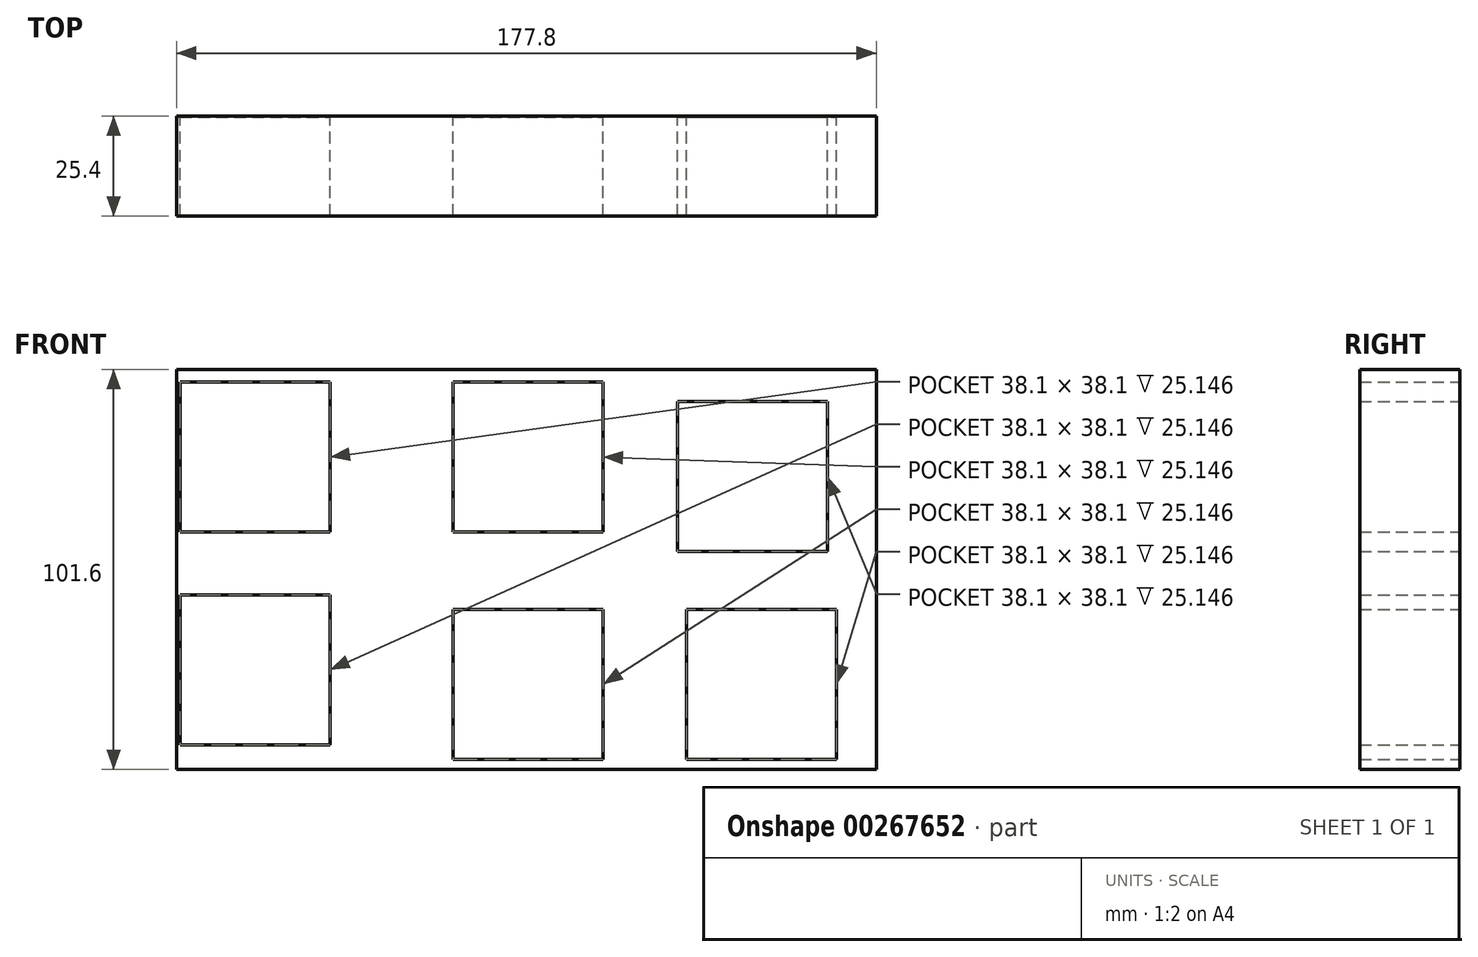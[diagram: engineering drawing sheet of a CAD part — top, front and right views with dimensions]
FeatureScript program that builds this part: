
annotation { "Feature Type Name" : "Feature", "Feature Type Description" : "" }
export const myFeature = defineFeature(function(context is Context, id is Id, definition is map)
    precondition{}
    {
        {
            var Q0;
            Q0=qCreatedBy(makeId("Front.planeOp"),FACE);
            var sketch = newSketch(context, id + "F0", { "sketchPlane" : qUnion([Q0])});
            skLineSegment(sketch, "E0.bottom", {"start": v(-82.35, 60.96) * mm, "end": v(95.45, 60.96) * mm});
            skLineSegment(sketch, "E0.top", {"start": v(-82.35, -40.64) * mm, "end": v(95.45, -40.64) * mm});
            skLineSegment(sketch, "E0.left", {"start": v(-82.35, 60.96) * mm, "end": v(-82.35, -40.64) * mm});
            skLineSegment(sketch, "E0.right", {"start": v(95.45, 60.96) * mm, "end": v(95.45, -40.64) * mm});
            skLineSegment(sketch, "E1.bottom", {"start": v(-81.47, 57.78) * mm, "end": v(-43.37, 57.78) * mm});
            skLineSegment(sketch, "E1.top", {"start": v(-81.47, 19.68) * mm, "end": v(-43.37, 19.68) * mm});
            skLineSegment(sketch, "E1.left", {"start": v(-81.47, 57.78) * mm, "end": v(-81.47, 19.68) * mm});
            skLineSegment(sketch, "E1.right", {"start": v(-43.37, 57.78) * mm, "end": v(-43.37, 19.68) * mm});
            skLineSegment(sketch, "E2.bottom", {"start": v(-81.47, 3.74) * mm, "end": v(-43.37, 3.74) * mm});
            skLineSegment(sketch, "E2.top", {"start": v(-81.47, -34.36) * mm, "end": v(-43.37, -34.36) * mm});
            skLineSegment(sketch, "E2.left", {"start": v(-81.47, 3.74) * mm, "end": v(-81.47, -34.36) * mm});
            skLineSegment(sketch, "E2.right", {"start": v(-43.37, 3.74) * mm, "end": v(-43.37, -34.36) * mm});
            skLineSegment(sketch, "E3.bottom", {"start": v(-12.03, 57.78) * mm, "end": v(26.07, 57.78) * mm});
            skLineSegment(sketch, "E3.top", {"start": v(-12.03, 19.68) * mm, "end": v(26.07, 19.68) * mm});
            skLineSegment(sketch, "E3.left", {"start": v(-12.03, 57.78) * mm, "end": v(-12.03, 19.68) * mm});
            skLineSegment(sketch, "E3.right", {"start": v(26.07, 57.78) * mm, "end": v(26.07, 19.68) * mm});
            skLineSegment(sketch, "E4.bottom", {"start": v(-12.03, 0) * mm, "end": v(26.07, 0) * mm});
            skLineSegment(sketch, "E4.top", {"start": v(-12.03, -38.1) * mm, "end": v(26.07, -38.1) * mm});
            skLineSegment(sketch, "E4.left", {"start": v(-12.03, 0) * mm, "end": v(-12.03, -38.1) * mm});
            skLineSegment(sketch, "E4.right", {"start": v(26.07, 0) * mm, "end": v(26.07, -38.1) * mm});
            skLineSegment(sketch, "E5.bottom", {"start": v(47.18, 0) * mm, "end": v(85.28, 0) * mm});
            skLineSegment(sketch, "E5.top", {"start": v(47.18, -38.1) * mm, "end": v(85.28, -38.1) * mm});
            skLineSegment(sketch, "E5.left", {"start": v(47.18, 0) * mm, "end": v(47.18, -38.1) * mm});
            skLineSegment(sketch, "E5.right", {"start": v(85.28, 0) * mm, "end": v(85.28, -38.1) * mm});
            skLineSegment(sketch, "E6.bottom", {"start": v(44.88, 52.9) * mm, "end": v(82.98, 52.9) * mm});
            skLineSegment(sketch, "E6.top", {"start": v(44.88, 14.8) * mm, "end": v(82.98, 14.8) * mm});
            skLineSegment(sketch, "E6.left", {"start": v(44.88, 52.9) * mm, "end": v(44.88, 14.8) * mm});
            skLineSegment(sketch, "E6.right", {"start": v(82.98, 52.9) * mm, "end": v(82.98, 14.8) * mm});
            skSolve(sketch);
        }
        {
            var Q0;
            Q0=makeQuery(id+"F0.imprint","IMPRINT",FACE,{"disambiguationData":[TD([[makeQuery(id+"F0.imprint","IMPRINT",EDGE,{"derivedFrom":sQuery(id+"F0.wireOp",EDGE,"E0.bottom")}),-1.0]])]});
            extrude(context, id + "F1", {"entities" : qUnion([Q0]), "depth" : 25.4 * mm});
        }
        {
            var Q0;
            Q0=makeQuery(id+"F0.imprint","IMPRINT",FACE,{"disambiguationData":[TD([[makeQuery(id+"F0.imprint","IMPRINT",EDGE,{"derivedFrom":sQuery(id+"F0.wireOp",EDGE,"E1.bottom")}),-1.0]])]});
            var Q1;
            Q1=makeQuery(id+"F0.imprint","IMPRINT",FACE,{"disambiguationData":[TD([[makeQuery(id+"F0.imprint","IMPRINT",EDGE,{"derivedFrom":sQuery(id+"F0.wireOp",EDGE,"E3.bottom")}),-1.0]])]});
            var Q2;
            Q2=makeQuery(id+"F0.imprint","IMPRINT",FACE,{"disambiguationData":[TD([[makeQuery(id+"F0.imprint","IMPRINT",EDGE,{"derivedFrom":sQuery(id+"F0.wireOp",EDGE,"E6.bottom")}),-1.0]])]});
            var Q3;
            Q3=makeQuery(id+"F0.imprint","IMPRINT",FACE,{"disambiguationData":[TD([[makeQuery(id+"F0.imprint","IMPRINT",EDGE,{"derivedFrom":sQuery(id+"F0.wireOp",EDGE,"E5.bottom")}),-1.0]])]});
            var Q4;
            Q4=makeQuery(id+"F0.imprint","IMPRINT",FACE,{"disambiguationData":[TD([[makeQuery(id+"F0.imprint","IMPRINT",EDGE,{"derivedFrom":sQuery(id+"F0.wireOp",EDGE,"E4.bottom")}),-1.0]])]});
            var Q5;
            Q5=makeQuery(id+"F0.imprint","IMPRINT",FACE,{"disambiguationData":[TD([[makeQuery(id+"F0.imprint","IMPRINT",EDGE,{"derivedFrom":sQuery(id+"F0.wireOp",EDGE,"E2.bottom")}),-1.0]])]});
            extrude(context, id + "F2", {"entities" : qUnion([Q0, Q1, Q2, Q3, Q4, Q5]), "operationType" : NewBodyOperationType.ADD, "depth" : 0.25 * mm});
        }
    });
